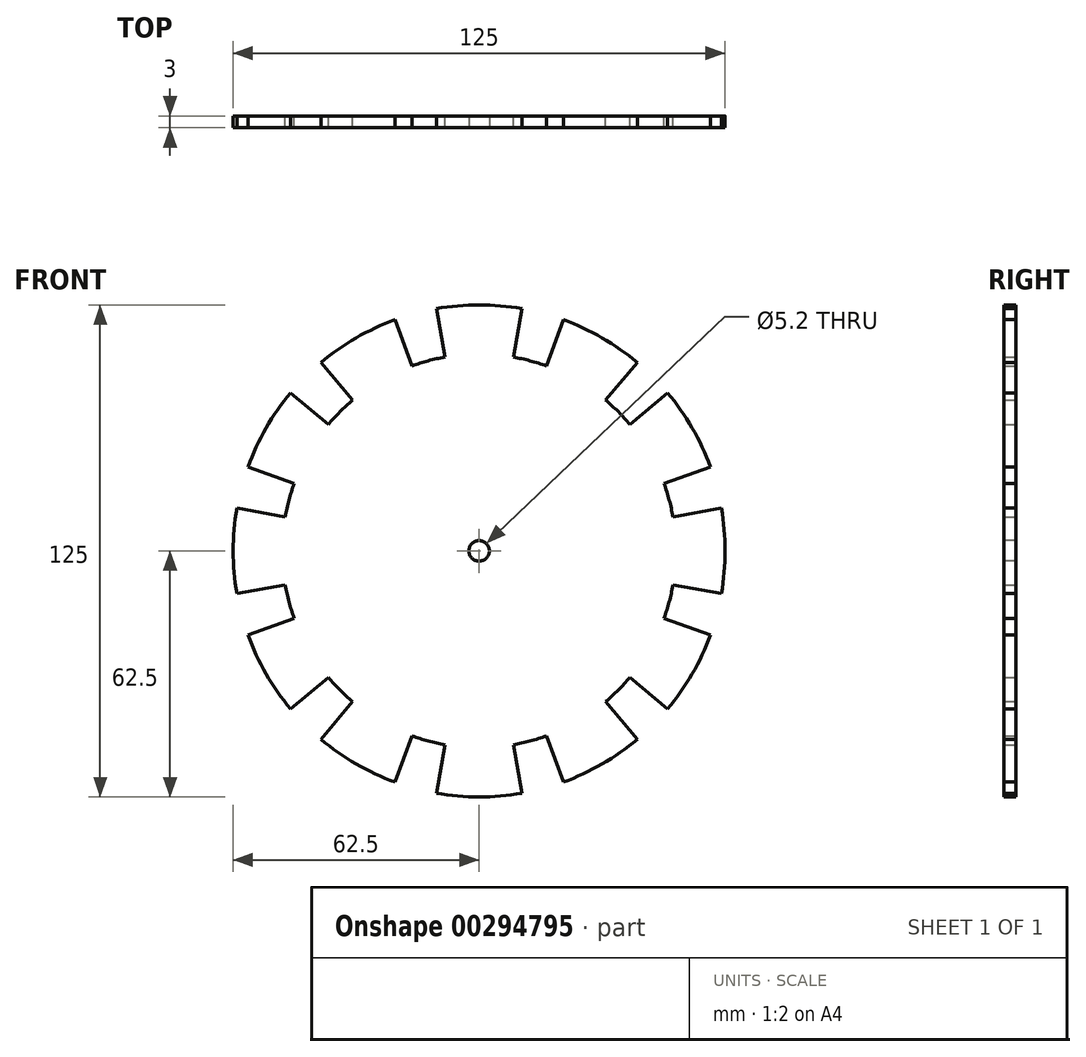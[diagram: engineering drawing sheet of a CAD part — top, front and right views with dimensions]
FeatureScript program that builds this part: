
annotation { "Feature Type Name" : "Feature", "Feature Type Description" : "" }
export const myFeature = defineFeature(function(context is Context, id is Id, definition is map)
    precondition{}
    {
        {
            var Q0;
            Q0=qCreatedBy(makeId("Front.planeOp"),FACE);
            var sketch = newSketch(context, id + "F0", { "sketchPlane" : qUnion([Q0])});
            skCircle(sketch, "E0", {"center": v(0, 0) * mm, "radius": 50 * mm});
            skArc(sketch, "E1", {"start": v(-21.38, 58.73) * mm, "mid": v(-31.25, 54.13) * mm, "end": v(-40.17, 47.88) * mm});
            skLineSegment(sketch, "E2", {"start": v(0, 62.5) * mm, "end": v(0, -62.5) * mm});
            skLineSegment(sketch, "E3", {"start": v(-62.5, 0) * mm, "end": v(62.5, 0) * mm});
            skLineSegment(sketch, "E4", {"start": v(0, 0) * mm, "end": v(31.25, 54.13) * mm});
            skLineSegment(sketch, "E5", {"start": v(0, 0) * mm, "end": v(54.13, 31.25) * mm});
            skLineSegment(sketch, "E6", {"start": v(0, 0) * mm, "end": v(54.13, -31.25) * mm});
            skLineSegment(sketch, "E7", {"start": v(0, 0) * mm, "end": v(31.25, -54.13) * mm});
            skLineSegment(sketch, "E8", {"start": v(0, 0) * mm, "end": v(-31.25, 54.13) * mm});
            skLineSegment(sketch, "E9", {"start": v(0, 0) * mm, "end": v(-54.13, 31.25) * mm});
            skLineSegment(sketch, "E10", {"start": v(0, 0) * mm, "end": v(-54.13, -31.25) * mm});
            skLineSegment(sketch, "E11", {"start": v(0, 0) * mm, "end": v(-31.25, -54.13) * mm});
            skLineSegment(sketch, "E12", {"start": v(0, 0) * mm, "end": v(-10.85, 61.55) * mm});
            skLineSegment(sketch, "E13", {"start": v(10.85, 61.55) * mm, "end": v(0, 0) * mm});
            skLineSegment(sketch, "E14", {"start": v(0, 0) * mm, "end": v(21.38, 58.73) * mm});
            skLineSegment(sketch, "E15", {"start": v(40.17, 47.88) * mm, "end": v(0, 0) * mm});
            skLineSegment(sketch, "E16", {"start": v(0, 0) * mm, "end": v(47.88, 40.17) * mm});
            skLineSegment(sketch, "E17", {"start": v(58.73, 21.38) * mm, "end": v(0, 0) * mm});
            skLineSegment(sketch, "E18", {"start": v(0, 0) * mm, "end": v(61.55, 10.85) * mm});
            skLineSegment(sketch, "E19", {"start": v(0, 0) * mm, "end": v(58.73, -21.38) * mm});
            skLineSegment(sketch, "E20", {"start": v(47.88, -40.17) * mm, "end": v(0, 0) * mm});
            skLineSegment(sketch, "E21", {"start": v(0, 0) * mm, "end": v(61.55, -10.85) * mm});
            skLineSegment(sketch, "E22", {"start": v(0, 0) * mm, "end": v(40.17, -47.88) * mm});
            skLineSegment(sketch, "E23", {"start": v(21.38, -58.73) * mm, "end": v(0, 0) * mm});
            skLineSegment(sketch, "E24", {"start": v(0, 0) * mm, "end": v(10.85, -61.55) * mm});
            skLineSegment(sketch, "E25", {"start": v(-10.85, -61.55) * mm, "end": v(0, 0) * mm});
            skLineSegment(sketch, "E26", {"start": v(0, 0) * mm, "end": v(-21.38, -58.73) * mm});
            skLineSegment(sketch, "E27", {"start": v(-40.17, -47.88) * mm, "end": v(0, 0) * mm});
            skLineSegment(sketch, "E28", {"start": v(0, 0) * mm, "end": v(-47.88, -40.17) * mm});
            skLineSegment(sketch, "E29", {"start": v(-58.73, -21.38) * mm, "end": v(0, 0) * mm});
            skLineSegment(sketch, "E30", {"start": v(0, 0) * mm, "end": v(-61.55, -10.85) * mm});
            skLineSegment(sketch, "E31", {"start": v(0, 0) * mm, "end": v(-58.73, 21.38) * mm});
            skLineSegment(sketch, "E32", {"start": v(-47.88, 40.17) * mm, "end": v(0, 0) * mm});
            skLineSegment(sketch, "E33", {"start": v(0, 0) * mm, "end": v(-40.17, 47.88) * mm});
            skLineSegment(sketch, "E34", {"start": v(-21.38, 58.73) * mm, "end": v(0, 0) * mm});
            skArc(sketch, "E35.trimOffspring", {"start": v(10.85, 61.55) * mm, "mid": v(0, 62.5) * mm, "end": v(-10.85, 61.55) * mm});
            skArc(sketch, "E36.trimOffspring", {"start": v(40.17, 47.88) * mm, "mid": v(31.25, 54.13) * mm, "end": v(21.38, 58.73) * mm});
            skArc(sketch, "E37.trimOffspring", {"start": v(58.73, 21.38) * mm, "mid": v(54.13, 31.25) * mm, "end": v(47.88, 40.17) * mm});
            skArc(sketch, "E38.trimOffspring", {"start": v(61.55, -10.85) * mm, "mid": v(62.5, 0) * mm, "end": v(61.55, 10.85) * mm});
            skArc(sketch, "E39.trimOffspring", {"start": v(47.88, -40.17) * mm, "mid": v(54.13, -31.25) * mm, "end": v(58.73, -21.38) * mm});
            skArc(sketch, "E40.trimOffspring", {"start": v(21.38, -58.73) * mm, "mid": v(31.25, -54.13) * mm, "end": v(40.17, -47.88) * mm});
            skArc(sketch, "E41.trimOffspring", {"start": v(-10.85, -61.55) * mm, "mid": v(0, -62.5) * mm, "end": v(10.85, -61.55) * mm});
            skArc(sketch, "E42.trimOffspring", {"start": v(-40.17, -47.88) * mm, "mid": v(-31.25, -54.13) * mm, "end": v(-21.38, -58.73) * mm});
            skArc(sketch, "E43.trimOffspring", {"start": v(-58.73, -21.38) * mm, "mid": v(-54.13, -31.25) * mm, "end": v(-47.88, -40.17) * mm});
            skArc(sketch, "E44.trimOffspring", {"start": v(-61.55, 10.85) * mm, "mid": v(-62.5, 0) * mm, "end": v(-61.55, -10.85) * mm});
            skArc(sketch, "E45.trimOffspring", {"start": v(-47.88, 40.17) * mm, "mid": v(-54.13, 31.25) * mm, "end": v(-58.73, 21.38) * mm});
            skLineSegment(sketch, "E46", {"start": v(-61.55, 10.85) * mm, "end": v(0, 0) * mm});
            skSolve(sketch);
        }
        {
            var Q0;
            Q0=qSketchRegion(id+"F0",true);
            extrude(context, id + "F1", {"entities" : qUnion([Q0]), "depth" : 3 * mm});
        }
        {
            var Q0;
            Q0=makeQuery(id+"F1.opExtrude","CAP_FACE",FACE,{"disambiguationData":[OSD([sQuery(id+"F0.wireOp",EDGE,"E0"),sQuery(id+"F0.wireOp",EDGE,"E1"),sQuery(id+"F0.wireOp",EDGE,"E12"),sQuery(id+"F0.wireOp",EDGE,"E13"),sQuery(id+"F0.wireOp",EDGE,"E14"),sQuery(id+"F0.wireOp",EDGE,"E15"),sQuery(id+"F0.wireOp",EDGE,"E16"),sQuery(id+"F0.wireOp",EDGE,"E17"),sQuery(id+"F0.wireOp",EDGE,"E18"),sQuery(id+"F0.wireOp",EDGE,"E19"),sQuery(id+"F0.wireOp",EDGE,"E20"),sQuery(id+"F0.wireOp",EDGE,"E21"),sQuery(id+"F0.wireOp",EDGE,"E22"),sQuery(id+"F0.wireOp",EDGE,"E23"),sQuery(id+"F0.wireOp",EDGE,"E24"),sQuery(id+"F0.wireOp",EDGE,"E25"),sQuery(id+"F0.wireOp",EDGE,"E26"),sQuery(id+"F0.wireOp",EDGE,"E27"),sQuery(id+"F0.wireOp",EDGE,"E28"),sQuery(id+"F0.wireOp",EDGE,"E29"),sQuery(id+"F0.wireOp",EDGE,"E30"),sQuery(id+"F0.wireOp",EDGE,"E31"),sQuery(id+"F0.wireOp",EDGE,"E32"),sQuery(id+"F0.wireOp",EDGE,"E33"),sQuery(id+"F0.wireOp",EDGE,"E34"),sQuery(id+"F0.wireOp",EDGE,"E35.trimOffspring"),sQuery(id+"F0.wireOp",EDGE,"E36.trimOffspring"),sQuery(id+"F0.wireOp",EDGE,"E37.trimOffspring"),sQuery(id+"F0.wireOp",EDGE,"E38.trimOffspring"),sQuery(id+"F0.wireOp",EDGE,"E39.trimOffspring"),sQuery(id+"F0.wireOp",EDGE,"E40.trimOffspring"),sQuery(id+"F0.wireOp",EDGE,"E41.trimOffspring"),sQuery(id+"F0.wireOp",EDGE,"E42.trimOffspring"),sQuery(id+"F0.wireOp",EDGE,"E43.trimOffspring"),sQuery(id+"F0.wireOp",EDGE,"E44.trimOffspring"),sQuery(id+"F0.wireOp",EDGE,"E45.trimOffspring"),sQuery(id+"F0.wireOp",EDGE,"E46")])],"isStart":false});
            var sketch = newSketch(context, id + "F2", { "sketchPlane" : qUnion([Q0])});
            skCircle(sketch, "E47", {"center": v(0, 0) * mm, "radius": 2.6 * mm});
            skSolve(sketch);
        }
        {
            var Q0;
            Q0=qSketchRegion(id+"F2",true);
            extrude(context, id + "F3", {"entities" : qUnion([Q0]), "operationType" : NewBodyOperationType.REMOVE, "endBound" : BoundingType.THROUGH_ALL, "oppositeDirection" : true, "depth" : 25 * mm});
        }
    });
